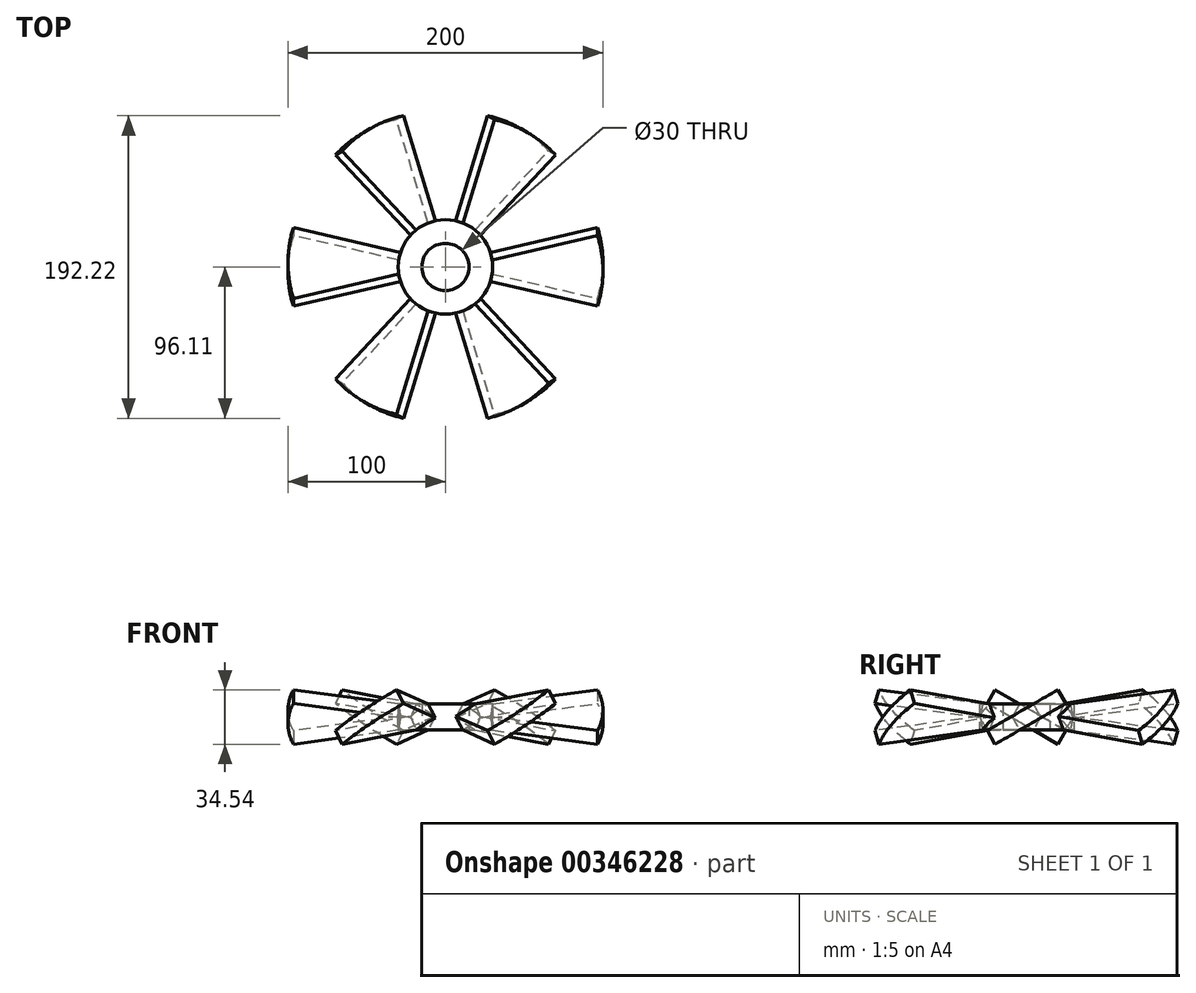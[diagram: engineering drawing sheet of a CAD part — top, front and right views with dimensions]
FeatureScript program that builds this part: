
annotation { "Feature Type Name" : "Feature", "Feature Type Description" : "" }
export const myFeature = defineFeature(function(context is Context, id is Id, definition is map)
    precondition{}
    {
        {
            var Q0;
            Q0=qCreatedBy(makeId("Top.planeOp"),FACE);
            var sketch = newSketch(context, id + "F0", { "sketchPlane" : qUnion([Q0])});
            skCircle(sketch, "E0", {"center": v(0, 0) * mm, "radius": 30 * mm});
            skCircle(sketch, "E1", {"center": v(0, 0) * mm, "radius": 15 * mm});
            skCircle(sketch, "E2", {"center": v(0, 0) * mm, "radius": 100 * mm});
            skLineSegment(sketch, "E3", {"start": v(0, 0) * mm, "end": v(15, 0) * mm});
            skLineSegment(sketch, "E4", {"start": v(0, 0) * mm, "end": v(96.6, 25.88) * mm});
            skLineSegment(sketch, "E5.MirrorCS", {"start": v(0, 0) * mm, "end": v(96.6, -25.88) * mm});
            skSolve(sketch);
        }
        {
            var Q0;
            {var subQ0=sQuery(id+"F0.wireOp",EDGE,"E4");var subQ1=sQuery(id+"F0.wireOp",EDGE,"E0");var subQ2=makeQuery(id+"F0.imprint","INTERSECT",VERTEX,{"derivedFrom":[subQ1,subQ0]});Q0=makeQuery(id+"F0.imprint","IMPRINT",FACE,{"disambiguationData":[TD([[makeQuery(id+"F0.imprint","IMPRINT",EDGE,{"disambiguationData":[TD([[subQ2,1.0]])],"derivedFrom":subQ1}),-1.0]])]});}
            var Q1;
            {var subQ0=sQuery(id+"F0.wireOp",EDGE,"E4");var subQ1=sQuery(id+"F0.wireOp",EDGE,"E0");var subQ2=makeQuery(id+"F0.imprint","INTERSECT",VERTEX,{"derivedFrom":[subQ1,subQ0]});Q1=makeQuery(id+"F0.imprint","IMPRINT",FACE,{"disambiguationData":[TD([[makeQuery(id+"F0.imprint","IMPRINT",EDGE,{"disambiguationData":[TD([[subQ2,1.0]])],"derivedFrom":subQ1}),1.0]])]});}
            extrude(context, id + "F1", {"entities" : qUnion([Q0, Q1]), "depth" : 5 * mm, "hasSecondDirection" : true, "secondDirectionOppositeDirection" : true, "secondDirectionDepth" : 5 * mm});
        }
        {
            var Q0;
            Q0=makeQuery(id+"F1.opExtrude","SWEPT_BODY",BODY,{"disambiguationData":[OSD([sQuery(id+"F0.wireOp",EDGE,"E1"),sQuery(id+"F0.wireOp",EDGE,"E2"),sQuery(id+"F0.wireOp",EDGE,"E4"),sQuery(id+"F0.wireOp",EDGE,"E5.MirrorCS")])]});
            var Q1;
            Q1=sQuery(id+"F0.wireOp",EDGE,"E3");
            transform(context, id + "F2", {"entities" : qUnion([Q0]), "transformType" : TransformType.ROTATION, "transformAxis" : qUnion([Q1]), "angle" : 30 * degree, "makeCopy" : false});
        }
        {
            var Q0;
            {var subQ0=sQuery(id+"F0.wireOp",EDGE,"E4");var subQ1=sQuery(id+"F0.wireOp",EDGE,"E0");var subQ2=makeQuery(id+"F0.imprint","INTERSECT",VERTEX,{"derivedFrom":[subQ1,subQ0]});Q0=makeQuery(id+"F0.imprint","IMPRINT",FACE,{"disambiguationData":[TD([[makeQuery(id+"F0.imprint","IMPRINT",EDGE,{"disambiguationData":[TD([[subQ2,-1.0]])],"derivedFrom":subQ1}),1.0]])]});}
            var Q1;
            {var subQ0=sQuery(id+"F0.wireOp",EDGE,"E4");var subQ1=sQuery(id+"F0.wireOp",EDGE,"E1");var subQ2=makeQuery(id+"F0.imprint","INTERSECT",VERTEX,{"derivedFrom":[subQ1,subQ0]});Q1=makeQuery(id+"F0.imprint","IMPRINT",FACE,{"disambiguationData":[TD([[makeQuery(id+"F0.imprint","IMPRINT",EDGE,{"disambiguationData":[TD([[subQ2,-1.0]])],"derivedFrom":subQ1}),1.0]])]});}
            var Q2;
            {var subQ0=sQuery(id+"F0.wireOp",EDGE,"E3");Q2=makeQuery(id+"F0.imprint","IMPRINT",FACE,{"disambiguationData":[TD([[makeQuery(id+"F0.imprint","IMPRINT",EDGE,{"derivedFrom":subQ0}),-1.0]])]});}
            var Q3;
            {var subQ0=sQuery(id+"F0.wireOp",EDGE,"E3");Q3=makeQuery(id+"F0.imprint","IMPRINT",FACE,{"disambiguationData":[TD([[makeQuery(id+"F0.imprint","IMPRINT",EDGE,{"derivedFrom":subQ0}),1.0]])]});}
            var Q4;
            {var subQ0=sQuery(id+"F0.wireOp",EDGE,"E4");var subQ1=sQuery(id+"F0.wireOp",EDGE,"E0");var subQ2=makeQuery(id+"F0.imprint","INTERSECT",VERTEX,{"derivedFrom":[subQ1,subQ0]});Q4=makeQuery(id+"F0.imprint","IMPRINT",FACE,{"disambiguationData":[TD([[makeQuery(id+"F0.imprint","IMPRINT",EDGE,{"disambiguationData":[TD([[subQ2,1.0]])],"derivedFrom":subQ1}),1.0]])]});}
            extrude(context, id + "F3", {"entities" : qUnion([Q0, Q1, Q2, Q3, Q4]), "operationType" : NewBodyOperationType.REMOVE, "oppositeDirection" : true, "depth" : 25 * mm, "hasSecondDirection" : true, "secondDirectionOppositeDirection" : false, "secondDirectionDepth" : 25 * mm});
        }
        {
            var Q0;
            Q0=qCreatedBy(makeId("Front.planeOp"),FACE);
            var sketch = newSketch(context, id + "F4", { "sketchPlane" : qUnion([Q0])});
            skLineSegment(sketch, "E6", {"start": v(0, 0) * mm, "end": v(0, 44.4) * mm});
            skSolve(sketch);
        }
        {
            var Q0;
            Q0=makeQuery(id+"F1.opExtrude","SWEPT_BODY",BODY,{"disambiguationData":[OSD([sQuery(id+"F0.wireOp",EDGE,"E1"),sQuery(id+"F0.wireOp",EDGE,"E2"),sQuery(id+"F0.wireOp",EDGE,"E4"),sQuery(id+"F0.wireOp",EDGE,"E5.MirrorCS")])]});
            var Q1;
            Q1=sQuery(id+"F4.wireOp",EDGE,"E6");
            circularPattern(context, id + "F5", {"entities" : qUnion([Q0]), "axis" : qUnion([Q1]), "angle" : 360 * degree, "instanceCount" : 6, "equalSpace" : true});
        }
        {
            var Q0;
            {var subQ0=sQuery(id+"F0.wireOp",EDGE,"E4");var subQ1=sQuery(id+"F0.wireOp",EDGE,"E0");var subQ2=makeQuery(id+"F0.imprint","INTERSECT",VERTEX,{"derivedFrom":[subQ1,subQ0]});Q0=makeQuery(id+"F0.imprint","IMPRINT",FACE,{"disambiguationData":[TD([[makeQuery(id+"F0.imprint","IMPRINT",EDGE,{"disambiguationData":[TD([[subQ2,-1.0]])],"derivedFrom":subQ1}),1.0]])]});}
            var Q1;
            {var subQ0=sQuery(id+"F0.wireOp",EDGE,"E4");var subQ1=sQuery(id+"F0.wireOp",EDGE,"E0");var subQ2=makeQuery(id+"F0.imprint","INTERSECT",VERTEX,{"derivedFrom":[subQ1,subQ0]});Q1=makeQuery(id+"F0.imprint","IMPRINT",FACE,{"disambiguationData":[TD([[makeQuery(id+"F0.imprint","IMPRINT",EDGE,{"disambiguationData":[TD([[subQ2,1.0]])],"derivedFrom":subQ1}),1.0]])]});}
            var Q2;
            {var subQ0=sQuery(id+"F0.wireOp",EDGE,"E4");Q2=makeQuery(id+"F5.opPattern","COPY",VERTEX,{"derivedFrom":makeQuery(id+"F3.boolean.opBoolean","INTERSECT",VERTEX,{"derivedFrom":[makeQuery(id+"F1.opExtrude","CAP_FACE",FACE,{"disambiguationData":[OSD([sQuery(id+"F0.wireOp",EDGE,"E1"),sQuery(id+"F0.wireOp",EDGE,"E2"),subQ0,sQuery(id+"F0.wireOp",EDGE,"E5.MirrorCS")])],"isStart":false}),makeQuery(id+"F1.opExtrude","SWEPT_FACE",FACE,{"disambiguationData":[OSD([subQ0])]}),makeQuery(id+"F3.opExtrude","SWEPT_FACE",FACE,{"disambiguationData":[OSD([sQuery(id+"F0.wireOp",EDGE,"E0")])]})]}),"instanceName":"1"});}
            var Q3;
            {var subQ0=sQuery(id+"F0.wireOp",EDGE,"E5.MirrorCS");Q3=makeQuery(id+"F5.opPattern","COPY",VERTEX,{"derivedFrom":makeQuery(id+"F3.boolean.opBoolean","INTERSECT",VERTEX,{"derivedFrom":[makeQuery(id+"F1.opExtrude","CAP_FACE",FACE,{"disambiguationData":[OSD([sQuery(id+"F0.wireOp",EDGE,"E1"),sQuery(id+"F0.wireOp",EDGE,"E2"),sQuery(id+"F0.wireOp",EDGE,"E4"),subQ0])],"isStart":true}),makeQuery(id+"F1.opExtrude","SWEPT_FACE",FACE,{"disambiguationData":[OSD([subQ0])]}),makeQuery(id+"F3.opExtrude","SWEPT_FACE",FACE,{"disambiguationData":[OSD([sQuery(id+"F0.wireOp",EDGE,"E0")])]})]}),"instanceName":"5"});}
            extrude(context, id + "F6", {"entities" : qUnion([Q0, Q1]), "endBound" : BoundingType.UP_TO_VERTEX, "endBoundEntityVertex" : qUnion([Q2]), "depth" : 25 * mm, "hasSecondDirection" : true, "secondDirectionBound" : SecondDirectionBoundingType.UP_TO_VERTEX, "secondDirectionOppositeDirection" : true, "secondDirectionBoundEntityVertex" : qUnion([Q3]), "secondDirectionDepth" : 25 * mm});
        }
    });
